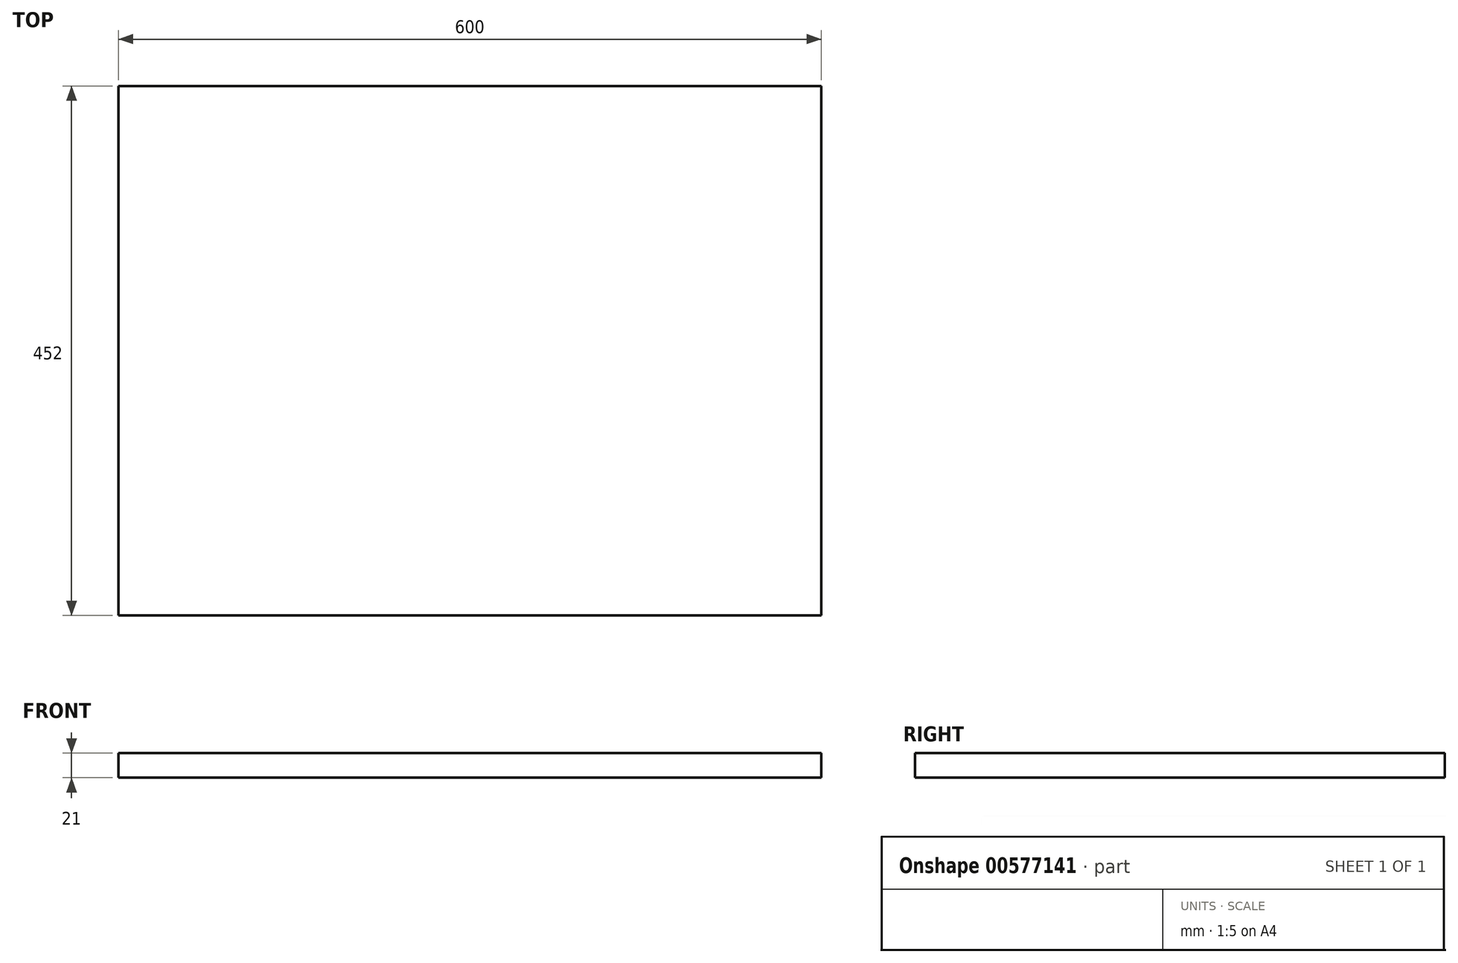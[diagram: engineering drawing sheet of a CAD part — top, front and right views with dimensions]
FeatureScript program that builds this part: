
annotation { "Feature Type Name" : "Feature", "Feature Type Description" : "" }
export const myFeature = defineFeature(function(context is Context, id is Id, definition is map)
    precondition{}
    {
        {
            var Q0;
            Q0=qCreatedBy(makeId("Top.planeOp"),FACE);
            var sketch = newSketch(context, id + "F0", { "sketchPlane" : qUnion([Q0])});
            skLineSegment(sketch, "E0.bottom", {"start": v(-300.3, 154.36) * mm, "end": v(299.7, 154.36) * mm});
            skLineSegment(sketch, "E0.top", {"start": v(-300.3, -297.64) * mm, "end": v(299.7, -297.64) * mm});
            skLineSegment(sketch, "E0.left", {"start": v(-300.3, 154.36) * mm, "end": v(-300.3, -297.64) * mm});
            skLineSegment(sketch, "E0.right", {"start": v(299.7, 154.36) * mm, "end": v(299.7, -297.64) * mm});
            skSolve(sketch);
        }
        {
            var Q0;
            Q0 = qSketchRegion(id + "F0", true);
            extrude(context, id + "F1", {"entities" : qUnion([Q0]), "depth" : 21 * mm, "offsetDistance" : 25 * mm});
        }
    });
